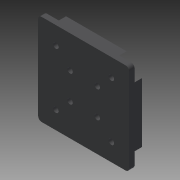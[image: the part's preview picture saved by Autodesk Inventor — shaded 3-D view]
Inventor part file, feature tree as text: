
AUTODESK INVENTOR PART (.ipt)
format: ipt  version: 2015 (Build 190159000, 159)  size: 144,384 bytes
history: native  units: mm
features: extrude x2, other x1, fillet x1
ambient origin geometry x8: Origin, YZ Plane, XZ Plane, XY Plane, X Axis, Y Axis, Z Axis, Center Point
bodies: Solid1 (feature_tree)
feature tree (4):
  other  "Grund"
  extrude  "Extrusion1"  Depth=50.0mm
  extrude  "Extrusion2"  Depth=50.0mm
  fillet  "Fillet1"  Radius=3.0mm
